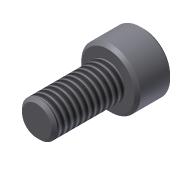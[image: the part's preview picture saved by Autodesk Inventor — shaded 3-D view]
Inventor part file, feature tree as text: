
AUTODESK INVENTOR PART (.ipt)
format: ipt  version: 2011 SP1 (Build 150282100, 282)  size: 110,592 bytes
history: native  units: in
note: dims shown in document units (in); Inventor stores cm internally (conversion verified against a paired STEP export)
features: extrude x3, sketch x3, thread x1, chamfer x1
ambient origin geometry x8: Origin, YZ Plane, XZ Plane, XY Plane, X Axis, Y Axis, Z Axis, Center Point
bodies: Solid1 (feature_tree)
feature tree (8):
  extrude  "Extrusion1"  Depth=0.4724in TaperAngle=0.0deg
  extrude  "Extrusion2"  Depth=0.2362in TaperAngle=0.0deg
  extrude  "Extrusion3"  Depth=0.1181in TaperAngle=0.0deg
  thread  "Thread1"  [1 undecoded]
  chamfer  "Chamfer1"  Distance=0.02in Angle=45.0deg
  sketch  "Sketch1"  dims[d0=0.2362in d1=0.4724in d2=0.0in]
  sketch  "Sketch2"  dims[d3=0.3937in d4=0.2362in d5=0.0in]
  sketch  "Sketch3"  dims[d6=0.1969in d7=0.1181in d8=0.0in d9=1.0in d10=0.0in d11=0.02in d12=0.125in d13=45.0deg]
note: 1 required parameter value undecoded (feature->parameter linkage not recoverable at this tier; creation-order binding heuristic only, values carry confidence <= 0.55)
